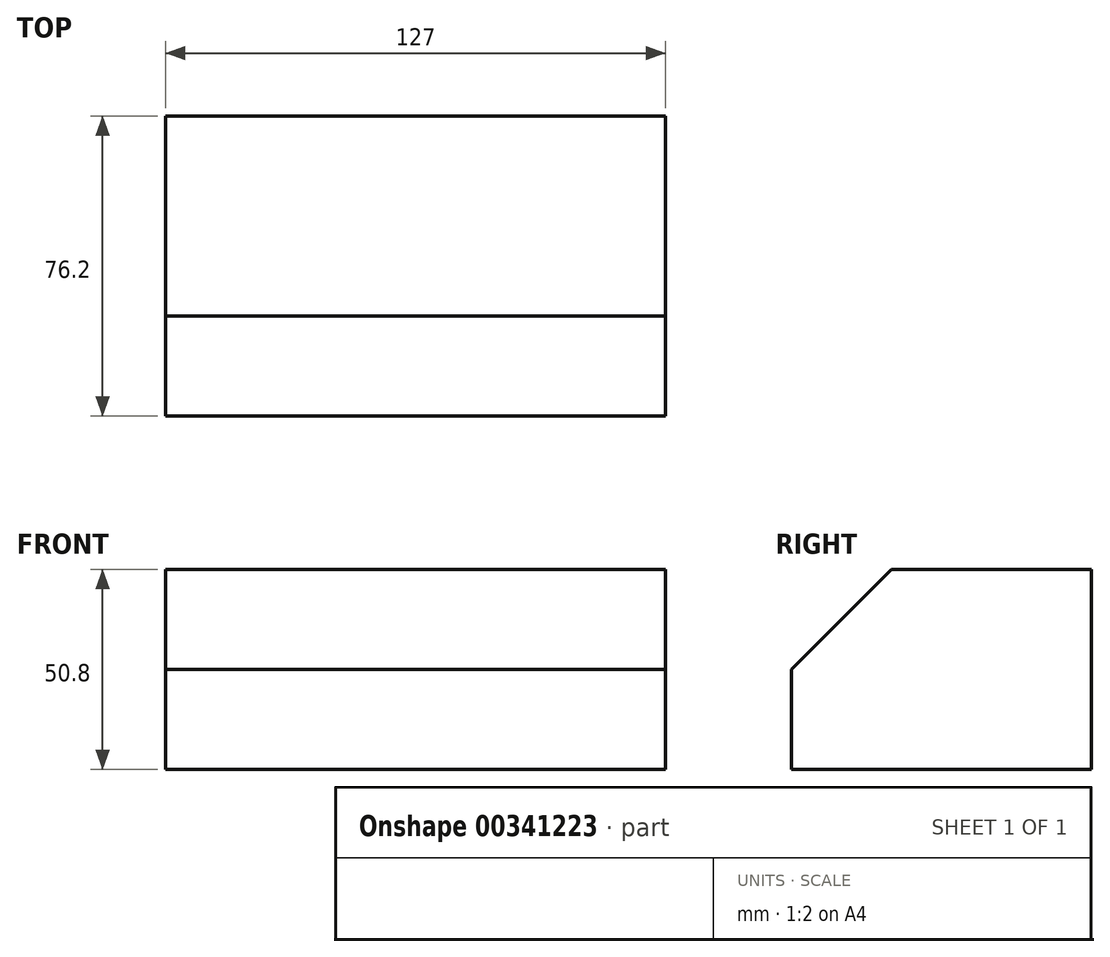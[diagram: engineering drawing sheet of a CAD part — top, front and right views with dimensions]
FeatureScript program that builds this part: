
annotation { "Feature Type Name" : "Feature", "Feature Type Description" : "" }
export const myFeature = defineFeature(function(context is Context, id is Id, definition is map)
    precondition{}
    {
        {
            var Q0;
            Q0=qCreatedBy(makeId("Right.planeOp"),FACE);
            var sketch = newSketch(context, id + "F0", { "sketchPlane" : qUnion([Q0])});
            skLineSegment(sketch, "E0", {"start": v(0, 0) * mm, "end": v(0, 25.4) * mm});
            skLineSegment(sketch, "E1", {"start": v(0, 25.4) * mm, "end": v(25.4, 50.8) * mm});
            skLineSegment(sketch, "E2", {"start": v(25.4, 50.8) * mm, "end": v(76.2, 50.8) * mm});
            skLineSegment(sketch, "E3", {"start": v(76.2, 50.8) * mm, "end": v(76.2, 0) * mm});
            skLineSegment(sketch, "E4", {"start": v(76.2, 0) * mm, "end": v(0, 0) * mm});
            skSolve(sketch);
        }
        {
            var Q0;
            Q0 = qSketchRegion(id + "F0", true);
            extrude(context, id + "F1", {"entities" : qUnion([Q0]), "depth" : 127 * mm});
        }
    });
